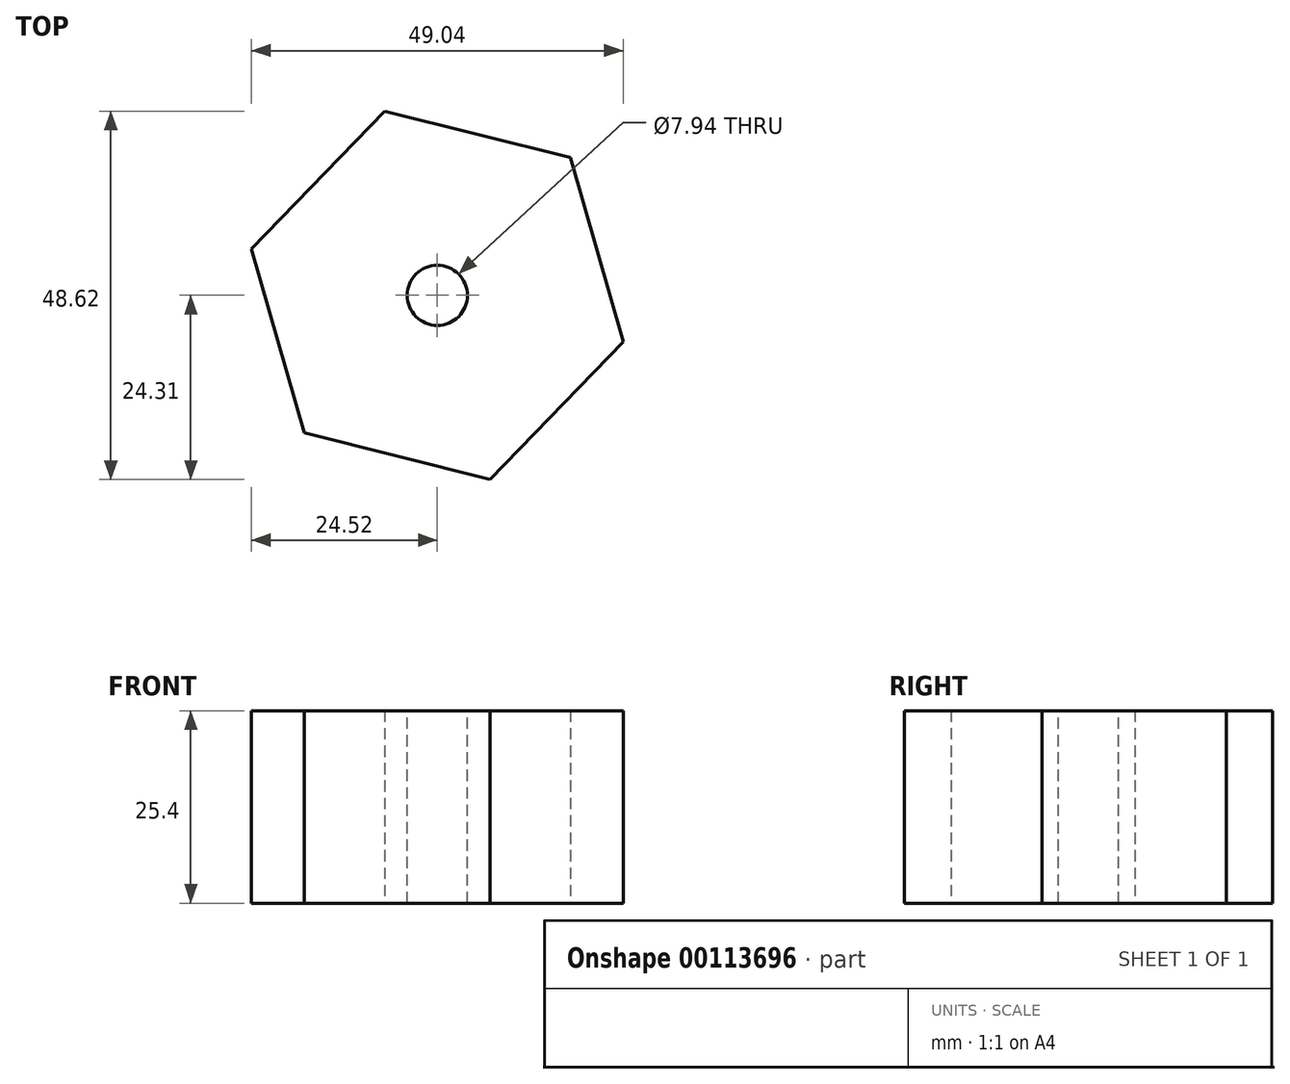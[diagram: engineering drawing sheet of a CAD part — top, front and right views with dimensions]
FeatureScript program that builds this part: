
annotation { "Feature Type Name" : "Feature", "Feature Type Description" : "" }
export const myFeature = defineFeature(function(context is Context, id is Id, definition is map)
    precondition{}
    {
        {
            var Q0;
            Q0=qCreatedBy(makeId("Top.planeOp"),FACE);
            var sketch = newSketch(context, id + "F0", { "sketchPlane" : qUnion([Q0])});
            skCircle(sketch, "E0.cCircle", {"center": v(0, 0) * mm, "radius": 21.9 * mm, "construction": true});
            skLineSegment(sketch, "E0.0", {"start": v(24.52, -6.14) * mm, "end": v(6.94, -24.3) * mm});
            skLineSegment(sketch, "E0.1", {"start": v(6.94, -24.3) * mm, "end": v(-17.58, -18.17) * mm});
            skLineSegment(sketch, "E0.2", {"start": v(-17.58, -18.17) * mm, "end": v(-24.52, 6.14) * mm});
            skLineSegment(sketch, "E0.3", {"start": v(-24.52, 6.14) * mm, "end": v(-6.94, 24.3) * mm});
            skLineSegment(sketch, "E0.4", {"start": v(-6.94, 24.3) * mm, "end": v(17.58, 18.17) * mm});
            skLineSegment(sketch, "E0.5", {"start": v(17.58, 18.17) * mm, "end": v(24.52, -6.14) * mm});
            skPoint(sketch, "E0.0.midPoint", {"position": v(15.73, -15.22) * mm});
            skSolve(sketch);
        }
        {
            var Q0;
            Q0=makeQuery(id+"F0.imprint","IMPRINT",FACE,{"disambiguationData":[TD([[makeQuery(id+"F0.imprint","IMPRINT",EDGE,{"derivedFrom":sQuery(id+"F0.wireOp",EDGE,"E0.0")}),-1.0]])]});
            extrude(context, id + "F1", {"entities" : qUnion([Q0]), "depth" : 25.4 * mm});
        }
        {
            var Q0;
            Q0=makeQuery(id+"F1.opExtrude","CAP_FACE",FACE,{"disambiguationData":[OSD([sQuery(id+"F0.wireOp",EDGE,"E0.0"),sQuery(id+"F0.wireOp",EDGE,"E0.1"),sQuery(id+"F0.wireOp",EDGE,"E0.2"),sQuery(id+"F0.wireOp",EDGE,"E0.3"),sQuery(id+"F0.wireOp",EDGE,"E0.4"),sQuery(id+"F0.wireOp",EDGE,"E0.5")])],"isStart":false});
            var sketch = newSketch(context, id + "F2", { "sketchPlane" : qUnion([Q0])});
            skCircle(sketch, "E1", {"center": v(0, 0) * mm, "radius": 10.96 * mm});
            skSolve(sketch);
        }
        {
            var Q0;
            Q0=sQuery(id+"F2.wireOp",VERTEX,"E1.center");
            var Q1;
            Q1=makeQuery(id+"F1.opExtrude","SWEPT_BODY",BODY,{"disambiguationData":[OSD([sQuery(id+"F0.wireOp",EDGE,"E0.0"),sQuery(id+"F0.wireOp",EDGE,"E0.1"),sQuery(id+"F0.wireOp",EDGE,"E0.2"),sQuery(id+"F0.wireOp",EDGE,"E0.3"),sQuery(id+"F0.wireOp",EDGE,"E0.4"),sQuery(id+"F0.wireOp",EDGE,"E0.5")])]});
            hole(context, id + "F3", {"style" : HoleStyle.SIMPLE, "endStyle" : HoleEndStyle.THROUGH, "standardTappedOrClearance" : lookupTablePath({ "standard" : "ANSI", "engagement" : "75%", "pitch" : "16 tpi", "size" : "3/8", "type" : "Tapped" }), "standardBlindInLast" : lookupTablePath({ "standard" : "ANSI", "engagement" : "75%", "pitch" : "16 tpi", "size" : "3/8", "type" : "Tapped" }), "holeDiameter" : 7.94 * mm, "locations" : qUnion([Q0]), "scope" : qUnion([Q1]), "isTappedThrough" : true, "majorDiameter" : 9.53 * mm, "showTappedDepth" : true});
        }
    });
